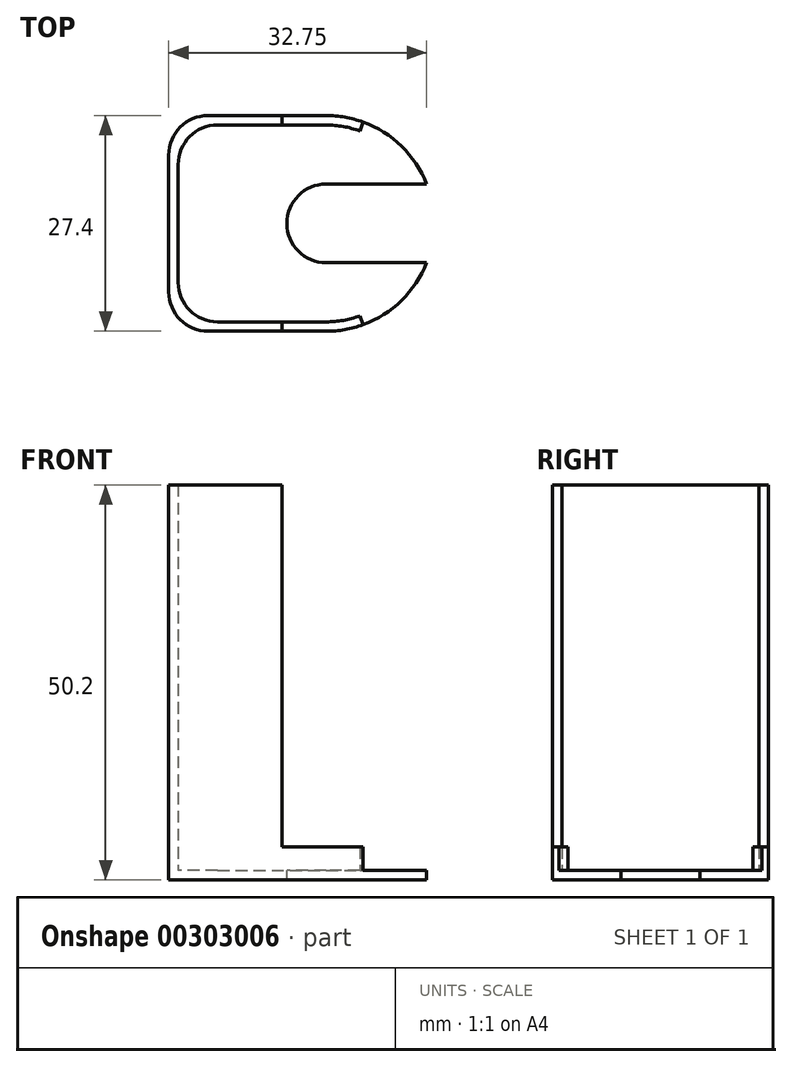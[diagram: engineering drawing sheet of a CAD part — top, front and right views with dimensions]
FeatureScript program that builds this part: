
annotation { "Feature Type Name" : "Feature", "Feature Type Description" : "" }
export const myFeature = defineFeature(function(context is Context, id is Id, definition is map)
    precondition{}
    {
        {
            var Q0;
            Q0=qCreatedBy(makeId("Top.planeOp"),FACE);
            var sketch = newSketch(context, id + "F0", { "sketchPlane" : qUnion([Q0])});
            skArc(sketch, "E0", {"start": v(0, -13.7) * mm, "mid": v(7.72, -11.32) * mm, "end": v(12.75, -5) * mm});
            skArc(sketch, "E1", {"start": v(0, -12.5) * mm, "mid": v(6.85, -10.46) * mm, "end": v(11.46, -5) * mm});
            skLineSegment(sketch, "E2.bottom", {"start": v(-15, 13.7) * mm, "end": v(0, 13.7) * mm});
            skLineSegment(sketch, "E2.top", {"start": v(-15, -13.7) * mm, "end": v(0, -13.7) * mm});
            skLineSegment(sketch, "E2.left", {"start": v(-20, 8.7) * mm, "end": v(-20, -8.7) * mm});
            skLineSegment(sketch, "E3.bottom", {"start": v(-13.8, 12.5) * mm, "end": v(0, 12.5) * mm});
            skLineSegment(sketch, "E3.top", {"start": v(-13.8, -12.5) * mm, "end": v(0, -12.5) * mm});
            skLineSegment(sketch, "E3.left", {"start": v(-18.8, 7.5) * mm, "end": v(-18.8, -7.5) * mm});
            skPoint(sketch, "E4.orphan", {"position": v(18.8, 12.5) * mm});
            skPoint(sketch, "E5.orphan", {"position": v(20, 13.7) * mm});
            skPoint(sketch, "E6.orphan", {"position": v(20, -13.7) * mm});
            skPoint(sketch, "E7.orphan", {"position": v(18.8, -12.5) * mm});
            skPoint(sketch, "E8.visualSharp", {"position": v(-18.8, 12.5) * mm});
            skArc(sketch, "E8.filletArc", {"start": v(-13.8, 12.5) * mm, "mid": v(-17.34, 11.04) * mm, "end": v(-18.8, 7.5) * mm});
            skPoint(sketch, "E9.visualSharp", {"position": v(-20, 13.7) * mm});
            skArc(sketch, "E9.filletArc", {"start": v(-15, 13.7) * mm, "mid": v(-18.54, 12.24) * mm, "end": v(-20, 8.7) * mm});
            skPoint(sketch, "E10.visualSharp", {"position": v(-18.8, -12.5) * mm});
            skArc(sketch, "E10.filletArc", {"start": v(-18.8, -7.5) * mm, "mid": v(-17.34, -11.04) * mm, "end": v(-13.8, -12.5) * mm});
            skPoint(sketch, "E11.visualSharp", {"position": v(-20, -13.7) * mm});
            skArc(sketch, "E11.filletArc", {"start": v(-20, -8.7) * mm, "mid": v(-18.54, -12.24) * mm, "end": v(-15, -13.7) * mm});
            skLineSegment(sketch, "E12", {"start": v(0, 0) * mm, "end": v(13.7, 0) * mm, "construction": true});
            skLineSegment(sketch, "E13", {"start": v(4.28, 11.75) * mm, "end": v(4.69, 12.87) * mm});
            skLineSegment(sketch, "E14", {"start": v(4.28, -11.75) * mm, "end": v(4.69, -12.87) * mm});
            skArc(sketch, "E15", {"start": v(0, 5) * mm, "mid": v(-5, 0) * mm, "end": v(0, -5) * mm});
            skLineSegment(sketch, "E16", {"start": v(0, 5) * mm, "end": v(12.75, 5) * mm});
            skLineSegment(sketch, "E17", {"start": v(0, -5) * mm, "end": v(12.75, -5) * mm});
            skArc(sketch, "E18.trimOffspring", {"start": v(11.46, 5) * mm, "mid": v(6.85, 10.46) * mm, "end": v(0, 12.5) * mm});
            skArc(sketch, "E19.trimOffspring", {"start": v(12.75, 5) * mm, "mid": v(7.72, 11.32) * mm, "end": v(0, 13.7) * mm});
            skSolve(sketch);
        }
        {
            var Q0;
            {var subQ0=sQuery(id+"F0.wireOp",EDGE,"E3.bottom");Q0=makeQuery(id+"F0.imprint","IMPRINT",FACE,{"disambiguationData":[TD([[makeQuery(id+"F0.imprint","IMPRINT",EDGE,{"derivedFrom":subQ0}),-1.0]])]});}
            var Q1;
            {var subQ0=sQuery(id+"F0.wireOp",EDGE,"E14");var subQ1=sQuery(id+"F0.wireOp",EDGE,"E1");var subQ2=makeQuery(id+"F0.imprint","INTERSECT",VERTEX,{"derivedFrom":[subQ1,subQ0]});Q1=makeQuery(id+"F0.imprint","IMPRINT",FACE,{"disambiguationData":[TD([[makeQuery(id+"F0.imprint","IMPRINT",EDGE,{"disambiguationData":[TD([[subQ2,-1.0]])],"derivedFrom":subQ1}),1.0]])]});}
            var Q2;
            {var subQ0=sQuery(id+"F0.wireOp",EDGE,"E13");var subQ1=sQuery(id+"F0.wireOp",EDGE,"E0");var subQ2=makeQuery(id+"F0.imprint","INTERSECT",VERTEX,{"derivedFrom":[subQ1,subQ0]});Q2=makeQuery(id+"F0.imprint","IMPRINT",FACE,{"disambiguationData":[TD([[makeQuery(id+"F0.imprint","IMPRINT",EDGE,{"disambiguationData":[TD([[subQ2,1.0]])],"derivedFrom":subQ1}),1.0]])]});}
            var Q3;
            {var subQ3=sQuery(id+"F0.wireOp",EDGE,"E2.bottom");Q3=makeQuery(id+"F0.imprint","IMPRINT",FACE,{"disambiguationData":[TD([[makeQuery(id+"F0.imprint","IMPRINT",EDGE,{"derivedFrom":subQ3}),-1.0]])]});}
            var Q4;
            {var subQ0=sQuery(id+"F0.wireOp",EDGE,"E13");Q4=makeQuery(id+"F0.imprint","IMPRINT",FACE,{"disambiguationData":[TD([[makeQuery(id+"F0.imprint","IMPRINT",EDGE,{"derivedFrom":subQ0}),-1.0]])]});}
            extrude(context, id + "F1", {"entities" : qUnion([Q0, Q1, Q2, Q3, Q4]), "oppositeDirection" : true, "depth" : 1.2 * mm, "offsetDistance" : 25 * mm});
        }
        {
            var Q0;
            {var subQ3=sQuery(id+"F0.wireOp",EDGE,"E2.bottom");Q0=makeQuery(id+"F0.imprint","IMPRINT",FACE,{"disambiguationData":[TD([[makeQuery(id+"F0.imprint","IMPRINT",EDGE,{"derivedFrom":subQ3}),-1.0]])]});}
            extrude(context, id + "F2", {"entities" : qUnion([Q0]), "operationType" : NewBodyOperationType.ADD, "depth" : 49 * mm, "offsetDistance" : 25 * mm});
        }
        {
            var Q0;
            Q0=makeQuery(id+"F2.opExtrude","CAP_FACE",FACE,{"disambiguationData":[OSD([sQuery(id+"F0.wireOp",EDGE,"E0"),sQuery(id+"F0.wireOp",EDGE,"E1"),sQuery(id+"F0.wireOp",EDGE,"E2.bottom"),sQuery(id+"F0.wireOp",EDGE,"E2.top"),sQuery(id+"F0.wireOp",EDGE,"E2.left"),sQuery(id+"F0.wireOp",EDGE,"E3.bottom"),sQuery(id+"F0.wireOp",EDGE,"E3.top"),sQuery(id+"F0.wireOp",EDGE,"E3.left"),sQuery(id+"F0.wireOp",EDGE,"E8.filletArc"),sQuery(id+"F0.wireOp",EDGE,"E9.filletArc"),sQuery(id+"F0.wireOp",EDGE,"E10.filletArc"),sQuery(id+"F0.wireOp",EDGE,"E11.filletArc"),sQuery(id+"F0.wireOp",EDGE,"E13"),sQuery(id+"F0.wireOp",EDGE,"E14"),sQuery(id+"F0.wireOp",EDGE,"E18.trimOffspring"),sQuery(id+"F0.wireOp",EDGE,"E19.trimOffspring")])],"isStart":false});
            var sketch = newSketch(context, id + "F3", { "sketchPlane" : qUnion([Q0])});
            skCircle(sketch, "E20", {"center": v(0, 0) * mm, "radius": 13.7 * mm});
            skLineSegment(sketch, "E21", {"start": v(-5.6, 12.5) * mm, "end": v(-5.6, 13.7) * mm});
            skLineSegment(sketch, "E22", {"start": v(-5.6, -12.5) * mm, "end": v(-5.6, -13.7) * mm});
            skCircle(sketch, "E23", {"center": v(0, 0) * mm, "radius": 12.5 * mm});
            skSolve(sketch);
        }
        {
            var Q0;
            {var subQ3=sQuery(id+"F3.wireOp",EDGE,"E21");Q0=makeQuery(id+"F3.imprint","IMPRINT",FACE,{"disambiguationData":[TD([[makeQuery(id+"F3.imprint","IMPRINT",EDGE,{"derivedFrom":subQ3}),-1.0]])]});}
            var Q1;
            {var subQ0=makeQuery(id+"F2.opExtrude","CAP_EDGE",EDGE,{"disambiguationData":[OSD([sQuery(id+"F0.wireOp",EDGE,"E13")])],"isStart":false});Q1=makeQuery(id+"F3.imprint","IMPRINT",FACE,{"disambiguationData":[TD([[makeQuery(id+"F3.imprint","IMPRINT",EDGE,{"derivedFrom":subQ0}),1.0]])]});}
            var Q2;
            {var subQ3=makeQuery(id+"F2.opExtrude","CAP_EDGE",EDGE,{"disambiguationData":[OSD([sQuery(id+"F0.wireOp",EDGE,"E14")])],"isStart":false});Q2=makeQuery(id+"F3.imprint","IMPRINT",FACE,{"disambiguationData":[TD([[makeQuery(id+"F3.imprint","IMPRINT",EDGE,{"derivedFrom":subQ3}),-1.0]])]});}
            var Q3;
            {var subQ3=sQuery(id+"F3.wireOp",EDGE,"E22");Q3=makeQuery(id+"F3.imprint","IMPRINT",FACE,{"disambiguationData":[TD([[makeQuery(id+"F3.imprint","IMPRINT",EDGE,{"derivedFrom":subQ3}),1.0]])]});}
            extrude(context, id + "F4", {"entities" : qUnion([Q0, Q1, Q2, Q3]), "operationType" : NewBodyOperationType.REMOVE, "oppositeDirection" : true, "depth" : 46 * mm, "offsetDistance" : 25 * mm});
        }
    });
